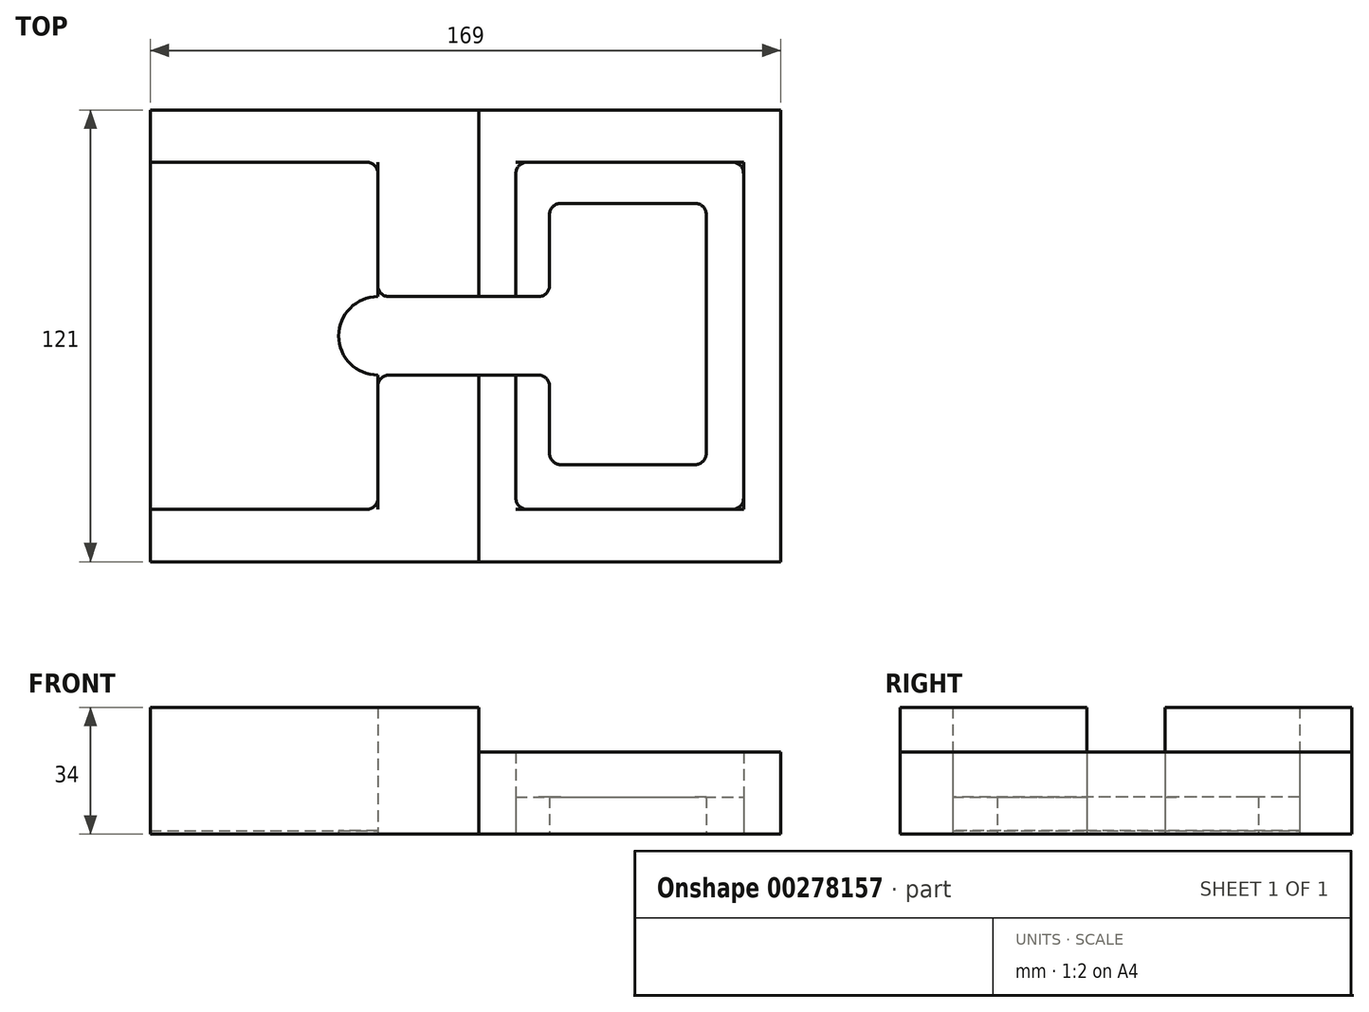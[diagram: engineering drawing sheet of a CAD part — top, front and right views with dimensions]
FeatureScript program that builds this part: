
annotation { "Feature Type Name" : "Feature", "Feature Type Description" : "" }
export const myFeature = defineFeature(function(context is Context, id is Id, definition is map)
    precondition{}
    {
        {
            var Q0;
            Q0=qCreatedBy(makeId("Top.planeOp"),FACE);
            var sketch = newSketch(context, id + "F0", { "sketchPlane" : qUnion([Q0])});
            skLineSegment(sketch, "E0.bottom", {"start": v(84.5, -60.5) * mm, "end": v(-84.5, -60.5) * mm});
            skLineSegment(sketch, "E0.top", {"start": v(84.5, 60.5) * mm, "end": v(-84.5, 60.5) * mm});
            skLineSegment(sketch, "E0.left", {"start": v(84.5, -60.5) * mm, "end": v(84.5, 60.5) * mm});
            skLineSegment(sketch, "E0.right", {"start": v(-84.5, -60.5) * mm, "end": v(-84.5, 60.5) * mm});
            skPoint(sketch, "E0.middle", {"position": v(0, 0) * mm});
            skLineSegment(sketch, "E1.bottom", {"start": v(-84.5, 46.5) * mm, "end": v(-23.5, 46.5) * mm});
            skLineSegment(sketch, "E1.top", {"start": v(-84.5, -46.5) * mm, "end": v(-23.5, -46.5) * mm});
            skLineSegment(sketch, "E1.left", {"start": v(-84.5, 46.5) * mm, "end": v(-84.5, -46.5) * mm});
            skLineSegment(sketch, "E1.right", {"start": v(-23.5, 46.5) * mm, "end": v(-23.5, 10.5) * mm});
            skLineSegment(sketch, "E2.bottom", {"start": v(-23.5, 10.5) * mm, "end": v(3.5, 10.5) * mm});
            skLineSegment(sketch, "E2.top", {"start": v(-23.5, -10.5) * mm, "end": v(3.5, -10.5) * mm});
            skLineSegment(sketch, "E3.trimOffspring", {"start": v(-23.5, -10.5) * mm, "end": v(-23.5, -46.5) * mm});
            skLineSegment(sketch, "E4.bottom", {"start": v(13.5, 46.5) * mm, "end": v(74.5, 46.5) * mm});
            skLineSegment(sketch, "E4.top", {"start": v(13.5, -46.5) * mm, "end": v(74.5, -46.5) * mm});
            skLineSegment(sketch, "E4.right", {"start": v(74.5, 46.5) * mm, "end": v(74.5, -46.5) * mm});
            skLineSegment(sketch, "E5.bottom", {"start": v(22.5, 35.5) * mm, "end": v(64.5, 35.5) * mm});
            skLineSegment(sketch, "E5.top", {"start": v(22.5, -34.5) * mm, "end": v(64.5, -34.5) * mm});
            skLineSegment(sketch, "E5.right", {"start": v(64.5, 35.5) * mm, "end": v(64.5, -34.5) * mm});
            skLineSegment(sketch, "E6", {"start": v(3.5, 10.5) * mm, "end": v(3.5, 60.5) * mm});
            skLineSegment(sketch, "E7", {"start": v(3.5, -10.5) * mm, "end": v(3.5, -60.5) * mm});
            skLineSegment(sketch, "E8", {"start": v(3.5, 10.5) * mm, "end": v(22.5, 10.5) * mm});
            skLineSegment(sketch, "E9", {"start": v(3.5, -10.5) * mm, "end": v(22.5, -10.5) * mm});
            skPoint(sketch, "E10", {"position": v(13.5, 10.5) * mm});
            skPoint(sketch, "E11", {"position": v(13.5, -10.5) * mm});
            skLineSegment(sketch, "E12", {"start": v(13.5, 46.5) * mm, "end": v(13.5, 10.5) * mm});
            skLineSegment(sketch, "E13", {"start": v(13.5, -46.5) * mm, "end": v(13.5, -10.5) * mm});
            skLineSegment(sketch, "E14", {"start": v(22.5, 35.5) * mm, "end": v(22.5, 10.5) * mm});
            skLineSegment(sketch, "E15", {"start": v(22.5, -34.5) * mm, "end": v(22.5, -10.5) * mm});
            skArc(sketch, "E16", {"start": v(-23.5, 10.5) * mm, "mid": v(-34, 0) * mm, "end": v(-23.5, -10.5) * mm});
            skSolve(sketch);
        }
        {
            var Q0;
            {var subQ0=sQuery(id+"F0.wireOp",EDGE,"E1.bottom");Q0=makeQuery(id+"F0.imprint","IMPRINT",FACE,{"disambiguationData":[TD([[makeQuery(id+"F0.imprint","IMPRINT",EDGE,{"derivedFrom":subQ0}),1.0]])]});}
            var Q1;
            {var subQ4=sQuery(id+"F0.wireOp",EDGE,"E1.top");Q1=makeQuery(id+"F0.imprint","IMPRINT",FACE,{"disambiguationData":[TD([[makeQuery(id+"F0.imprint","IMPRINT",EDGE,{"derivedFrom":subQ4}),-1.0]])]});}
            extrude(context, id + "F1", {"entities" : qUnion([Q0, Q1]), "depth" : 34 * mm});
        }
        {
            var Q0;
            Q0=makeQuery(id+"F0.imprint","IMPRINT",FACE,{"disambiguationData":[TD([[makeQuery(id+"F0.imprint","IMPRINT",EDGE,{"derivedFrom":sQuery(id+"F0.wireOp",EDGE,"E1.bottom")}),-1.0]])]});
            extrude(context, id + "F2", {"entities" : qUnion([Q0]), "depth" : .9 * mm});
        }
        {
            var Q0;
            Q0=makeQuery(id+"F0.imprint","IMPRINT",FACE,{"disambiguationData":[TD([[makeQuery(id+"F0.imprint","IMPRINT",EDGE,{"derivedFrom":sQuery(id+"F0.wireOp",EDGE,"E4.bottom")}),-1.0]])]});
            extrude(context, id + "F3", {"entities" : qUnion([Q0]), "operationType" : NewBodyOperationType.ADD, "depth" : 10 * mm});
        }
        {
            var Q0;
            {var subQ4=sQuery(id+"F0.wireOp",EDGE,"E0.left");Q0=makeQuery(id+"F0.imprint","IMPRINT",FACE,{"disambiguationData":[TD([[makeQuery(id+"F0.imprint","IMPRINT",EDGE,{"derivedFrom":subQ4}),1.0]])]});}
            extrude(context, id + "F4", {"entities" : qUnion([Q0]), "depth" : 22 * mm});
        }
        {
            var Q0;
            Q0=makeQuery(id+"F1.opExtrude","SWEPT_EDGE",EDGE,{"disambiguationData":[OSD([sQuery(id+"F0.wireOp",EDGE,"E1.bottom"),sQuery(id+"F0.wireOp",EDGE,"E1.right")])]});
            var Q1;
            Q1=makeQuery(id+"F1.opExtrude","SWEPT_EDGE",EDGE,{"disambiguationData":[OSD([sQuery(id+"F0.wireOp",EDGE,"E1.top"),sQuery(id+"F0.wireOp",EDGE,"E3.trimOffspring")])]});
            var Q2;
            Q2=makeQuery(id+"F3.opExtrude","SWEPT_EDGE",EDGE,{"disambiguationData":[OSD([sQuery(id+"F0.wireOp",EDGE,"E5.bottom"),sQuery(id+"F0.wireOp",EDGE,"E14")])]});
            var Q3;
            Q3=makeQuery(id+"F4.opExtrude","SWEPT_EDGE",EDGE,{"disambiguationData":[OSD([sQuery(id+"F0.wireOp",EDGE,"E4.bottom"),sQuery(id+"F0.wireOp",EDGE,"E12")])]});
            var Q4;
            Q4=makeQuery(id+"F3.opExtrude","SWEPT_EDGE",EDGE,{"disambiguationData":[OSD([sQuery(id+"F0.wireOp",EDGE,"E5.bottom"),sQuery(id+"F0.wireOp",EDGE,"E5.right")])]});
            var Q5;
            Q5=makeQuery(id+"F4.opExtrude","SWEPT_EDGE",EDGE,{"disambiguationData":[OSD([sQuery(id+"F0.wireOp",EDGE,"E4.bottom"),sQuery(id+"F0.wireOp",EDGE,"E4.right")])]});
            var Q6;
            Q6=makeQuery(id+"F3.opExtrude","SWEPT_EDGE",EDGE,{"disambiguationData":[OSD([sQuery(id+"F0.wireOp",EDGE,"E5.top"),sQuery(id+"F0.wireOp",EDGE,"E15")])]});
            var Q7;
            Q7=makeQuery(id+"F4.opExtrude","SWEPT_EDGE",EDGE,{"disambiguationData":[OSD([sQuery(id+"F0.wireOp",EDGE,"E4.top"),sQuery(id+"F0.wireOp",EDGE,"E13")])]});
            var Q8;
            Q8=makeQuery(id+"F3.opExtrude","SWEPT_EDGE",EDGE,{"disambiguationData":[OSD([sQuery(id+"F0.wireOp",EDGE,"E5.top"),sQuery(id+"F0.wireOp",EDGE,"E5.right")])]});
            var Q9;
            Q9=makeQuery(id+"F4.opExtrude","SWEPT_EDGE",EDGE,{"disambiguationData":[OSD([sQuery(id+"F0.wireOp",EDGE,"E4.top"),sQuery(id+"F0.wireOp",EDGE,"E4.right")])]});
            var Q10;
            Q10=makeQuery(id+"F1.opExtrude","SWEPT_EDGE",EDGE,{"disambiguationData":[OSD([sQuery(id+"F0.wireOp",EDGE,"E1.right"),sQuery(id+"F0.wireOp",EDGE,"E2.bottom"),sQuery(id+"F0.wireOp",EDGE,"3nwAGM5j-E6jq-qsvM-K4i5-g0Hie0WvUXQn")])]});
            var Q11;
            Q11=makeQuery(id+"F1.opExtrude","SWEPT_EDGE",EDGE,{"disambiguationData":[OSD([sQuery(id+"F0.wireOp",EDGE,"E2.top"),sQuery(id+"F0.wireOp",EDGE,"E3.trimOffspring"),sQuery(id+"F0.wireOp",EDGE,"3nwAGM5j-E6jq-qsvM-K4i5-g0Hie0WvUXQn")])]});
            var Q12;
            Q12=makeQuery(id+"F3.opExtrude","SWEPT_EDGE",EDGE,{"disambiguationData":[OSD([sQuery(id+"F0.wireOp",EDGE,"E8"),sQuery(id+"F0.wireOp",EDGE,"E14")])]});
            var Q13;
            Q13=makeQuery(id+"F3.opExtrude","SWEPT_EDGE",EDGE,{"disambiguationData":[OSD([sQuery(id+"F0.wireOp",EDGE,"E9"),sQuery(id+"F0.wireOp",EDGE,"E15")])]});
            fillet(context, id + "F5", {"entities" : qUnion([Q0, Q1, Q2, Q3, Q4, Q5, Q6, Q7, Q8, Q9, Q10, Q11, Q12, Q13]), "radius" : 3 * mm, "tangentPropagation" : true, "allowEdgeOverflow" : false});
        }
    });
